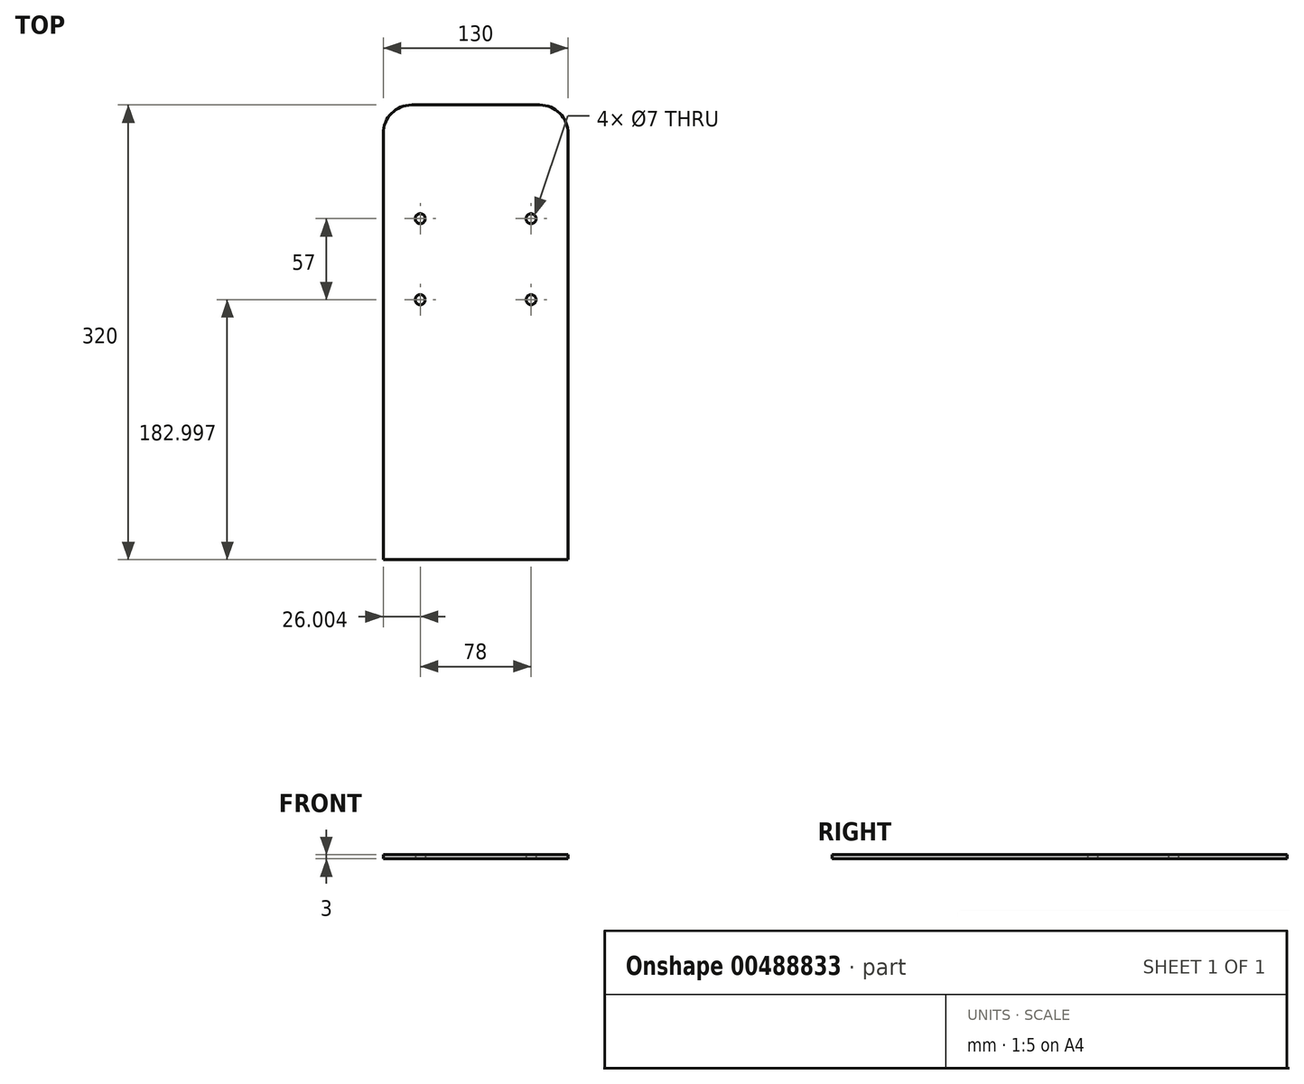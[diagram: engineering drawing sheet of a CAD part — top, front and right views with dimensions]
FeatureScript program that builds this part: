
annotation { "Feature Type Name" : "Feature", "Feature Type Description" : "" }
export const myFeature = defineFeature(function(context is Context, id is Id, definition is map)
    precondition{}
    {
        {
            var Q0;
            Q0=qCreatedBy(makeId("Top.planeOp"),FACE);
            var sketch = newSketch(context, id + "F0", { "sketchPlane" : qUnion([Q0])});
            skLineSegment(sketch, "E0.bottom", {"start": v(-52, 255.02) * mm, "end": v(38, 255.02) * mm});
            skLineSegment(sketch, "E0.top", {"start": v(-52, -64.98) * mm, "end": v(38, -64.98) * mm});
            skLineSegment(sketch, "E0.left", {"start": v(-72, 235.02) * mm, "end": v(-72, -89.98) * mm});
            skLineSegment(sketch, "E0.right", {"start": v(58, 235.02) * mm, "end": v(58, -74.98) * mm});
            skPoint(sketch, "E1.visualSharp", {"position": v(-72, -64.98) * mm});
            skPoint(sketch, "E2.visualSharp", {"position": v(58, -64.98) * mm});
            skLineSegment(sketch, "E3.top", {"start": v(-72, -64.98) * mm, "end": v(-52, -64.98) * mm});
            skLineSegment(sketch, "E3.left", {"start": v(-72, -64.98) * mm, "end": v(-72, -89.98) * mm});
            skLineSegment(sketch, "E4.bottom", {"start": v(38, -64.98) * mm, "end": v(58, -64.98) * mm});
            skLineSegment(sketch, "E4.right", {"start": v(58, -74.98) * mm, "end": v(58, -64.98) * mm});
            skPoint(sketch, "E5.visualSharp", {"position": v(-72, 255.02) * mm});
            skArc(sketch, "E5.filletArc", {"start": v(-52, 255.02) * mm, "mid": v(-66.15, 249.16) * mm, "end": v(-72, 235.02) * mm});
            skPoint(sketch, "E6.visualSharp", {"position": v(58, 255.02) * mm});
            skArc(sketch, "E6.filletArc", {"start": v(58, 235.02) * mm, "mid": v(52.14, 249.16) * mm, "end": v(38, 255.02) * mm});
            skCircle(sketch, "E7", {"center": v(-46, 175.02) * mm, "radius": 3.5 * mm});
            skCircle(sketch, "E8", {"center": v(32, 175.02) * mm, "radius": 3.5 * mm});
            skCircle(sketch, "E9", {"center": v(-46, 118.02) * mm, "radius": 3.5 * mm});
            skCircle(sketch, "E10", {"center": v(32, 118.02) * mm, "radius": 3.5 * mm});
            skSolve(sketch);
        }
        {
            var Q0;
            Q0=makeQuery(id+"F0.imprint","IMPRINT",FACE,{"disambiguationData":[TD([[makeQuery(id+"F0.imprint","IMPRINT",EDGE,{"derivedFrom":sQuery(id+"F0.wireOp",EDGE,"E0.bottom")}),-1.0]])]});
            extrude(context, id + "F1", {"entities" : qUnion([Q0]), "depth" : 3 * mm});
        }
    });
